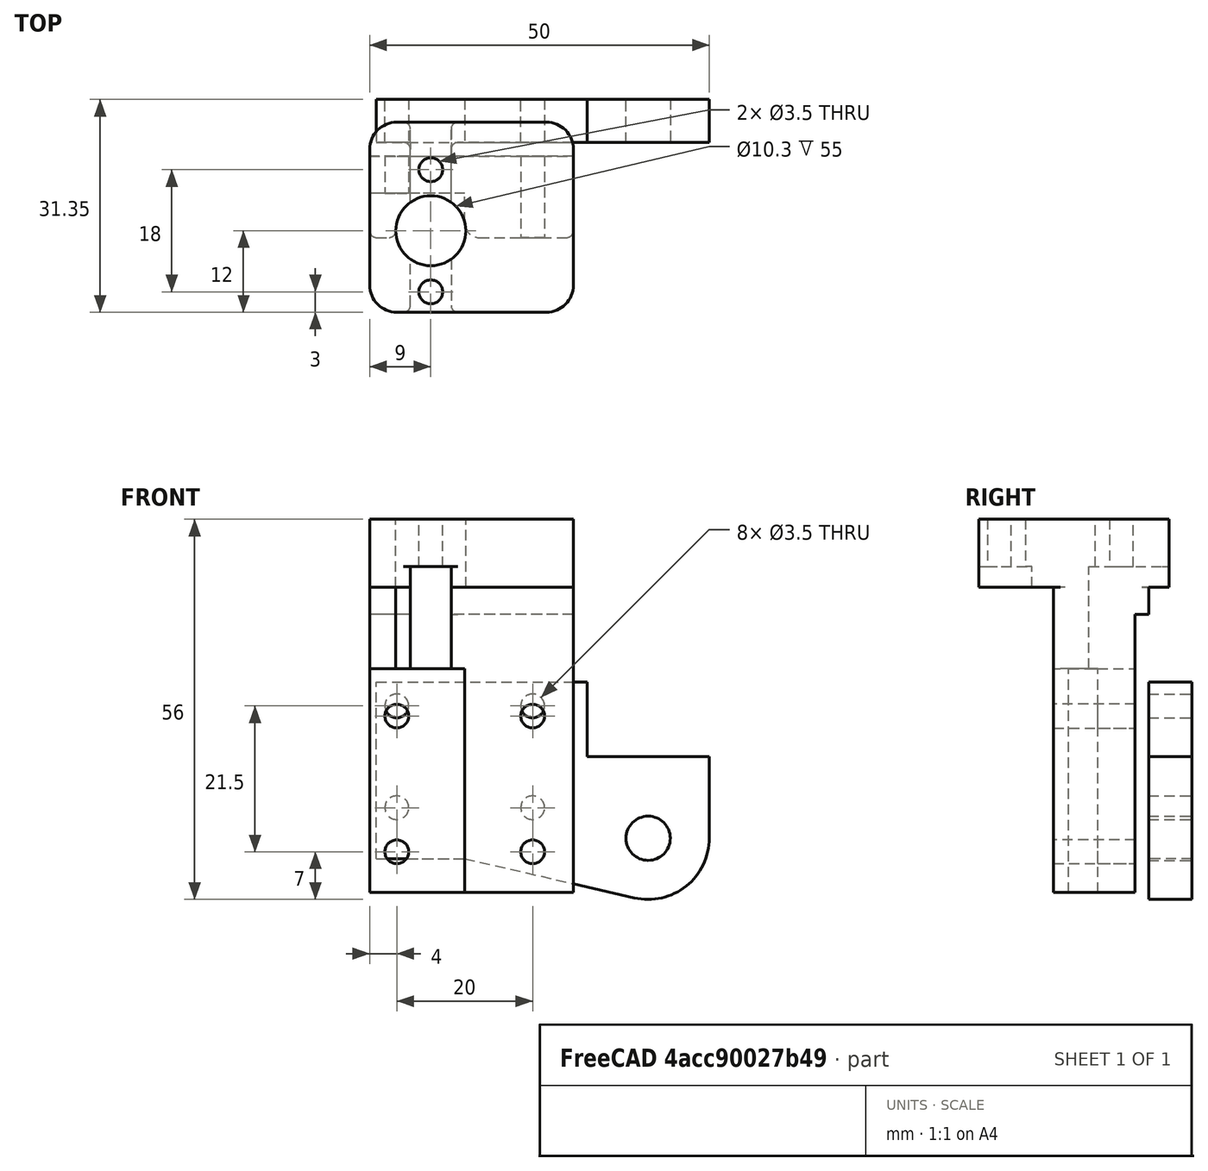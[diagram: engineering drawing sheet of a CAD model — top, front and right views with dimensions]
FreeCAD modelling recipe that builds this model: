
FCSTD DOCUMENT  (FreeCAD 0.19R)
Label: ZnutHolder_H2
License: All rights reserved
LicenseURL: http://en.wikipedia.org/wiki/All_rights_reserved
objects: Sketcher::SketchObject×10, PartDesign::Pocket×7, PartDesign::Fillet×7, PartDesign::Pad×2, PartDesign::Body×2, Mesh::Feature×1
note: 44 computed .brp shape members not serialized (recipe doc carries the construction recipe); baked Part::Feature solids carry a one-line shape summary decoded from their .brp

FEATURE [Sketcher::SketchObject] Sketch
  FullyConstrained = false
  MapMode = 5
  Placement = pos=(0,0,0) rot=(1,0,0;1.5708rad)
  Support = -> [XZ_Plane]
  sketch-geometry (14):
    g0: Circle CenterX=-10 CenterY=7.5 CenterZ=0 NormalX=0 NormalY=0 NormalZ=1 AngleXU=0 Radius=1.75
    g1: Circle CenterX=10 CenterY=7.5 CenterZ=0 NormalX=0 NormalY=0 NormalZ=1 AngleXU=0 Radius=1.75
    g2: Circle CenterX=-10 CenterY=-7.5 CenterZ=0 NormalX=0 NormalY=0 NormalZ=1 AngleXU=0 Radius=1.75
    g3: Circle CenterX=10 CenterY=-7.5 CenterZ=0 NormalX=0 NormalY=0 NormalZ=1 AngleXU=0 Radius=1.75
    g4: LineSegment StartX=-13 StartY=11 StartZ=0 EndX=18 EndY=11 EndZ=0
    g5: LineSegment StartX=18 StartY=11 StartZ=0 EndX=18 EndY=0 EndZ=0
    g6: LineSegment StartX=18 StartY=0 StartZ=0 EndX=36 EndY=0 EndZ=0
    g7: LineSegment StartX=36 StartY=0 StartZ=0 EndX=36 EndY=-12 EndZ=0
    g8: LineSegment StartX=-13 StartY=-15 StartZ=0 EndX=-13 EndY=11 EndZ=0
    g9: LineSegment StartX=-13 StartY=-15 StartZ=0 EndX=0 EndY=-15 EndZ=0
    g10: LineSegment StartX=0 StartY=-15 StartZ=0 EndX=24.9743 EndY=-20.7691 EndZ=0
    g11: ArcOfCircle CenterX=27 CenterY=-12 CenterZ=0 NormalX=0 NormalY=0 NormalZ=1 AngleXU=0 Radius=9 StartAngle=4.48537 EndAngle=6.28319
    g12: Circle CenterX=27 CenterY=-12 CenterZ=0 NormalX=0 NormalY=0 NormalZ=1 AngleXU=0 Radius=3.25
    g13: LineSegment StartX=19 StartY=18.0628 StartZ=0 EndX=19 EndY=-24.6673 EndZ=0
  constraints (37):
    c: Symmetric(g0,g1,g-2)
    c: Symmetric(g3,g2,g-2)
    c: Symmetric(g3,g1,g-1)
    c: Diameter(g0) = 3.5
    c: Equal(g0,g1)
    c: Equal(g0,g2)
    c: Equal(g0,g3)
    c: Distance(g1,g0) = 20
    c: Distance(g3,g1) = 15
    c: Horizontal(g4)
    c: Coincident(g4,g5)
    c: Vertical(g5)
    c: Coincident(g5,g6)
    c: Horizontal(g6)
    c: Coincident(g6,g7)
    c: Vertical(g7)
    c: Vertical(g8)
    c: DistanceX(g4) = 18
    c: DistanceX(g4) = -13
    c: Coincident(g8,g9)
    c: PointOnObject(g9,g-2)
    c: Horizontal(g9)
    c: Coincident(g9,g10)
    c: Tangent(g7,g11) = 1.5708
    c: Coincident(g11,g7)
    c: Tangent(g11,g10) = -1.5708
    c: Coincident(g12,g11)
    c: Diameter(g12) = 6.5
    c: Diameter(g11) = 18
    c: Vertical(g13)
    c: DistanceX(g13) = 19
    c: Distance(g11,g13) = 8
    c: Distance(g11,g6) = 12
    c: PointOnObject(g5,g-1)
    c: Coincident(g8,g4)
    c: DistanceY(g4) = 11
    c: DistanceY(g8) = -15
FEATURE [PartDesign::Pad] Pad
  Direction = (1,1,1)
  Length = 6.35
  Length2 = 100
  Placement = pos=(0,0,0) rot=(1,0,0;1.5708rad)
  Profile = -> Sketch
  Type = 0
FEATURE [PartDesign::Body] Body  label="Tab"
  Group = -> [Sketch,Pad]
  Origin = -> Origin
  Placement = pos=(0,6.35,0) rot=(0,0,1;0rad)
  Tip = -> Pad
FEATURE [Sketcher::SketchObject] Sketch005  label="body"
  FullyConstrained = true
  MapMode = 5
  Placement = pos=(0,0,0) rot=(0.57735,0.57735,0.57735;2.0944rad)
  Support = -> [YZ_Plane001]
  sketch-geometry (8):
    g0: LineSegment StartX=0 StartY=-20 StartZ=0 EndX=0 EndY=25 EndZ=0
    g1: LineSegment StartX=0 StartY=25 StartZ=0 EndX=3 EndY=25 EndZ=0
    g2: LineSegment StartX=3 StartY=25 StartZ=0 EndX=3 EndY=35 EndZ=0
    g3: LineSegment StartX=3 StartY=35 StartZ=0 EndX=-25 EndY=35 EndZ=0
    g4: LineSegment StartX=-25 StartY=35 StartZ=0 EndX=-25 EndY=25 EndZ=0
    g5: LineSegment StartX=-25 StartY=25 StartZ=0 EndX=-14 EndY=25 EndZ=0
    g6: LineSegment StartX=-14 StartY=25 StartZ=0 EndX=-14 EndY=-20 EndZ=0
    g7: LineSegment StartX=-14 StartY=-20 StartZ=0 EndX=0 EndY=-20 EndZ=0
  constraints (24):
    c: PointOnObject(g0,g-2)
    c: PointOnObject(g0,g-2)
    c: Coincident(g0,g1)
    c: Coincident(g1,g2)
    c: Vertical(g2)
    c: Coincident(g2,g3)
    c: Horizontal(g3)
    c: Coincident(g3,g4)
    c: Vertical(g4)
    c: Coincident(g4,g5)
    c: Horizontal(g5)
    c: Coincident(g5,g6)
    c: Vertical(g6)
    c: Coincident(g6,g7)
    c: Coincident(g7,g0)
    c: Horizontal(g7)
    c: Distance(g4) = 10
    c: DistanceY(g2) = 35
    c: DistanceX(g4) = -25
    c: Distance(g7) = 14
    c: DistanceY(g0) = -20
    c: DistanceX(g2) = 3
    c: Horizontal(g1)
    c: Distance(g2) = 10
FEATURE [PartDesign::Pad] Pad001
  Direction = (1,1,1)
  Length = 16
  Length2 = 16
  Placement = pos=(0,0,0) rot=(0.57735,0.57735,0.57735;2.0944rad)
  Profile = -> Sketch005
  Type = 4
FEATURE [Sketcher::SketchObject] Sketch011  label="Carriage"
  FullyConstrained = false
  MapMode = 5
  Placement = pos=(0,0,0) rot=(1,0,0;1.5708rad)
  Support = -> [XZ_Plane001]
  sketch-geometry (4):
    g0: LineSegment StartX=-19.4447 StartY=17.5 StartZ=0 EndX=25.2288 EndY=17.5 EndZ=0
    g1: LineSegment StartX=25.2288 StartY=17.5 StartZ=0 EndX=25.2288 EndY=-17.5 EndZ=0
    g2: LineSegment StartX=25.2288 StartY=-17.5 StartZ=0 EndX=-19.4447 EndY=-17.5 EndZ=0
    g3: LineSegment StartX=-19.4447 StartY=-17.5 StartZ=0 EndX=-19.4447 EndY=17.5 EndZ=0
  constraints (10):
    c: Coincident(g0,g1)
    c: Coincident(g1,g2)
    c: Coincident(g2,g3)
    c: Coincident(g3,g0)
    c: Horizontal(g0)
    c: Horizontal(g2)
    c: Vertical(g1)
    c: Vertical(g3)
    c: DistanceY(g0) = 17.5
    c: Distance(g1) = 35
FEATURE [Sketcher::SketchObject] Sketch012  label="NutHole"
  FullyConstrained = true
  MapMode = 5
  Placement = pos=(-6e-14,3.5e-14,35) rot=(0,0,-1;1.5708rad)
  sketch-geometry (1):
    g0: Circle CenterX=13 CenterY=-5 CenterZ=0 NormalX=0 NormalY=0 NormalZ=1 AngleXU=0 Radius=5.15
  constraints (3):
    c: Diameter(g0) = 10.3
    c: DistanceY(g0) = -5
    c: DistanceX(g0) = 13
FEATURE [Sketcher::SketchObject] Sketch013  label="Nutscrews"
  FullyConstrained = true
  MapMode = 5
  Placement = pos=(-7.2e-14,3.9e-14,35) rot=(0,0,-1;1.5708rad)
  sketch-geometry (2):
    g0: Circle CenterX=4 CenterY=-5 CenterZ=0 NormalX=0 NormalY=0 NormalZ=1 AngleXU=0 Radius=1.75
    g1: Circle CenterX=22 CenterY=-5 CenterZ=0 NormalX=0 NormalY=0 NormalZ=1 AngleXU=0 Radius=1.75
  constraints (6):
    c: DistanceY(g1) = -5
    c: DistanceY(g0) = -5
    c: DistanceX(g1) = 22
    c: DistanceX(g0) = 4
    c: Diameter(g1) = 3.5
    c: Equal(g1,g0)
FEATURE [Sketcher::SketchObject] Sketch014
  ExternalGeometry = -> [Pad001]
  FullyConstrained = true
  MapMode = 5
  Placement = pos=(-1.11e-14,-25,8.3e-15) rot=(-0.57735,-0.57735,0.57735;4.18879rad)
  Support = -> [Pad001]
  sketch-geometry (4):
    g0: LineSegment StartX=-28 StartY=-2 StartZ=0 EndX=-13 EndY=-2 EndZ=0
    g1: LineSegment StartX=-13 StartY=-2 StartZ=0 EndX=-13 EndY=-8 EndZ=0
    g2: LineSegment StartX=-13 StartY=-8 StartZ=0 EndX=-28 EndY=-8 EndZ=0
    g3: LineSegment StartX=-28 StartY=-8 StartZ=0 EndX=-28 EndY=-2 EndZ=0
  constraints (12):
    c: Coincident(g0,g1)
    c: Coincident(g1,g2)
    c: Coincident(g2,g3)
    c: Coincident(g3,g0)
    c: Horizontal(g0)
    c: Horizontal(g2)
    c: Vertical(g1)
    c: Vertical(g3)
    c: Distance(g0,g-3) = 7
    c: Distance(g1) = 6
    c: DistanceY(g0) = -2
    c: Distance(g0) = 15
FEATURE [PartDesign::Pocket] Pocket
  BaseFeature = -> Pad001
  Length = 5
  Length2 = 100
  Placement = pos=(0,0,0) rot=(0.57735,0.57735,0.57735;2.0944rad)
  Profile = -> Sketch014
  Type = 1
FEATURE [PartDesign::Pocket] Pocket001
  BaseFeature = -> Pocket
  Length = 5
  Length2 = 100
  Placement = pos=(0,0,0) rot=(0.57735,0.57735,0.57735;2.0944rad)
  Profile = -> Sketch012
  Type = 1
FEATURE [PartDesign::Pocket] Pocket002
  BaseFeature = -> Pocket001
  Length = 7
  Length2 = 100
  Placement = pos=(0,0,0) rot=(0.57735,0.57735,0.57735;2.0944rad)
  Profile = -> Sketch013
  Type = 0
FEATURE [Sketcher::SketchObject] Sketch008  label="ScrewRelief"
  FullyConstrained = false
  MapMode = 5
  Placement = pos=(2.78e-14,-1.78e-14,-20) rot=(0.707107,0.707107,0;3.14159rad)
  Support = -> [Pocket002]
  sketch-geometry (4):
    g0: LineSegment StartX=-14.9077 StartY=0 StartZ=0 EndX=-7.5 EndY=0 EndZ=0
    g1: LineSegment StartX=-7.5 StartY=0 StartZ=0 EndX=-7.5 EndY=-16 EndZ=0
    g2: LineSegment StartX=-7.5 StartY=-16 StartZ=0 EndX=-14.9077 EndY=-16 EndZ=0
    g3: LineSegment StartX=-14.9077 StartY=-16 StartZ=0 EndX=-14.9077 EndY=0 EndZ=0
  constraints (11):
    c: Coincident(g0,g1)
    c: Coincident(g1,g2)
    c: Coincident(g2,g3)
    c: Coincident(g3,g0)
    c: Horizontal(g0)
    c: Horizontal(g2)
    c: Vertical(g1)
    c: Vertical(g3)
    c: Distance(g1) = 16
    c: DistanceY(g0) = 0
    c: DistanceX(g1) = -7.5
FEATURE [PartDesign::Pocket] Pocket003
  BaseFeature = -> Pocket002
  Length = 33
  Length2 = 100
  Placement = pos=(0,0,0) rot=(0.57735,0.57735,0.57735;2.0944rad)
  Profile = -> Sketch008
  Type = 0
FEATURE [Sketcher::SketchObject] Sketch007  label="ScrewHoles_rail"
  FullyConstrained = true
  MapMode = 5
  Placement = pos=(-6.2e-15,-14,2.33e-14) rot=(0.57735,0.57735,-0.57735;2.0944rad)
  Support = -> [Pocket003]
  sketch-geometry (8):
    g0: Circle CenterX=-6 CenterY=10 CenterZ=0 NormalX=0 NormalY=0 NormalZ=1 AngleXU=0 Radius=1.75
    g1: Circle CenterX=14 CenterY=10 CenterZ=0 NormalX=0 NormalY=0 NormalZ=1 AngleXU=0 Radius=1.75
    g2: Circle CenterX=-6 CenterY=-10 CenterZ=0 NormalX=0 NormalY=0 NormalZ=1 AngleXU=0 Radius=1.75
    g3: Circle CenterX=14 CenterY=-10 CenterZ=0 NormalX=0 NormalY=0 NormalZ=1 AngleXU=0 Radius=1.75
    g4: LineSegment StartX=-6 StartY=10 StartZ=0 EndX=-6 EndY=-10 EndZ=0
    g5: LineSegment StartX=-6 StartY=-10 StartZ=0 EndX=14 EndY=-10 EndZ=0
    g6: LineSegment StartX=14 StartY=-10 StartZ=0 EndX=14 EndY=10 EndZ=0
    g7: LineSegment StartX=14 StartY=10 StartZ=0 EndX=-6 EndY=10 EndZ=0
  constraints (19):
    c: Diameter(g0) = 3.5
    c: Equal(g0,g1)
    c: Equal(g0,g2)
    c: Equal(g0,g3)
    c: Coincident(g4,g0)
    c: Coincident(g4,g2)
    c: Coincident(g4,g5)
    c: Coincident(g5,g3)
    c: Coincident(g5,g6)
    c: Coincident(g6,g1)
    c: Coincident(g6,g7)
    c: Coincident(g7,g4)
    c: Equal(g4,g6)
    c: Equal(g7,g5)
    c: Distance(g7) = 20
    c: Distance(g6) = 20
    c: Perpendicular(g6,g5)
    c: Symmetric(g1,g3,g-1)
    c: DistanceX(g0) = -6
FEATURE [PartDesign::Pocket] Pocket004
  BaseFeature = -> Pocket003
  Length = 5
  Length2 = 100
  Placement = pos=(0,0,0) rot=(0.57735,0.57735,0.57735;2.0944rad)
  Profile = -> Sketch007
  Type = 1
FEATURE [Sketcher::SketchObject] Sketch015  label="backpocket"
  ExternalGeometry = -> [Pocket004]
  FullyConstrained = true
  MapMode = 5
  Placement = pos=(0,4e-14,0) rot=(0.57735,0.57735,0.57735;4.18879rad)
  Support = -> [Pocket004]
  sketch-geometry (4):
    g0: LineSegment StartX=-29.47 StartY=20 StartZ=0 EndX=21 EndY=20 EndZ=0
    g1: LineSegment StartX=21 StartY=20 StartZ=0 EndX=21 EndY=-20 EndZ=0
    g2: LineSegment StartX=21 StartY=-20 StartZ=0 EndX=-29.47 EndY=-20 EndZ=0
    g3: LineSegment StartX=-29.47 StartY=-20 StartZ=0 EndX=-29.47 EndY=20 EndZ=0
  constraints (11):
    c: Coincident(g0,g1)
    c: Coincident(g1,g2)
    c: Coincident(g2,g3)
    c: Coincident(g3,g0)
    c: Horizontal(g0)
    c: Horizontal(g2)
    c: Vertical(g1)
    c: Distance(g3) = 40
    c: Symmetric(g2,g0,g-1)
    c: Distance(g0) = 50.47
    c: Distance(g-3,g1) = 15
FEATURE [PartDesign::Pocket] Pocket005
  BaseFeature = -> Pocket004
  Length = 2
  Length2 = 100
  Placement = pos=(0,0,0) rot=(0.57735,0.57735,0.57735;2.0944rad)
  Profile = -> Sketch015
  Type = 0
FEATURE [Sketcher::SketchObject] Sketch016
  FullyConstrained = true
  MapMode = 5
  Placement = pos=(-8.35e-14,4.27e-14,35) rot=(0,0,-1;1.5708rad)
  Support = -> [Pocket005]
  sketch-geometry (4):
    g0: LineSegment StartX=-6.58 StartY=-14 StartZ=0 EndX=45.4 EndY=-14 EndZ=0
    g1: LineSegment StartX=45.4 StartY=-14 StartZ=0 EndX=45.4 EndY=-28.53 EndZ=0
    g2: LineSegment StartX=45.4 StartY=-28.53 StartZ=0 EndX=-6.58 EndY=-28.53 EndZ=0
    g3: LineSegment StartX=-6.58 StartY=-28.53 StartZ=0 EndX=-6.58 EndY=-14 EndZ=0
  constraints (12):
    c: Coincident(g0,g1)
    c: Coincident(g1,g2)
    c: Coincident(g2,g3)
    c: Coincident(g3,g0)
    c: Horizontal(g0)
    c: Horizontal(g2)
    c: Vertical(g1)
    c: Vertical(g3)
    c: DistanceY(g0) = -14
    c: DistanceX(g0) = -6.58
    c: Distance(g1) = 14.53
    c: DistanceX(g0) = 45.4
FEATURE [PartDesign::Pocket] Pocket006
  BaseFeature = -> Pocket005
  Length = 5
  Length2 = 100
  Placement = pos=(0,0,0) rot=(0.57735,0.57735,0.57735;2.0944rad)
  Profile = -> Sketch016
  Type = 1
FEATURE [PartDesign::Fillet] Fillet
  Base = -> Pocket006 [Edge37,Edge6,Edge64,Edge15]
  BaseFeature = -> Pocket006
  Placement = pos=(0,0,0) rot=(0.57735,0.57735,0.57735;2.0944rad)
  Radius = 4
  SupportTransform = false
FEATURE [PartDesign::Fillet] Fillet001
  Base = -> Fillet [Edge97,Edge94]
  BaseFeature = -> Fillet
  Placement = pos=(0,0,0) rot=(0.57735,0.57735,0.57735;2.0944rad)
  Radius = 1
  SupportTransform = false
FEATURE [PartDesign::Fillet] Fillet002
  Base = -> Fillet001 [Edge41]
  BaseFeature = -> Fillet001
  Placement = pos=(0,0,0) rot=(0.57735,0.57735,0.57735;2.0944rad)
  Radius = 2
  SupportTransform = false
FEATURE [PartDesign::Fillet] Fillet003
  Base = -> Fillet002 [Edge77,Edge15]
  BaseFeature = -> Fillet002
  Placement = pos=(0,0,0) rot=(0.57735,0.57735,0.57735;2.0944rad)
  Radius = 1
  SupportTransform = false
FEATURE [PartDesign::Fillet] Fillet004
  Base = -> Fillet003 [Edge52,Edge29]
  BaseFeature = -> Fillet003
  Placement = pos=(0,0,0) rot=(0.57735,0.57735,0.57735;2.0944rad)
  Radius = 1
  SupportTransform = false
FEATURE [PartDesign::Fillet] Fillet005
  Base = -> Fillet004 [Edge6,Edge64]
  BaseFeature = -> Fillet004
  Placement = pos=(0,0,0) rot=(0.57735,0.57735,0.57735;2.0944rad)
  Radius = 1
  SupportTransform = false
FEATURE [PartDesign::Fillet] Fillet006
  Base = -> Fillet005 [Edge81]
  BaseFeature = -> Fillet005
  Placement = pos=(0,0,0) rot=(0.57735,0.57735,0.57735;2.0944rad)
  Radius = 1
  SupportTransform = false
FEATURE [PartDesign::Body] Body001  label="LeadScrewMount"
  Group = -> [Sketch005,Pad001,Sketch007,Sketch008,Sketch011,Sketch012,Sketch013,Sketch014,Pocket,Pocket001,Pocket002,Pocket003,Pocket004,Sketch015,Pocket005,Sketch016,Pocket006,Fillet,Fillet001,Fillet002,Fillet003,Fillet004,Fillet005,Fillet006]
  Origin = -> Origin001
  Tip = -> Fillet006
FEATURE [Mesh::Feature] Mesh  label="Fillet006 (Meshed)"
